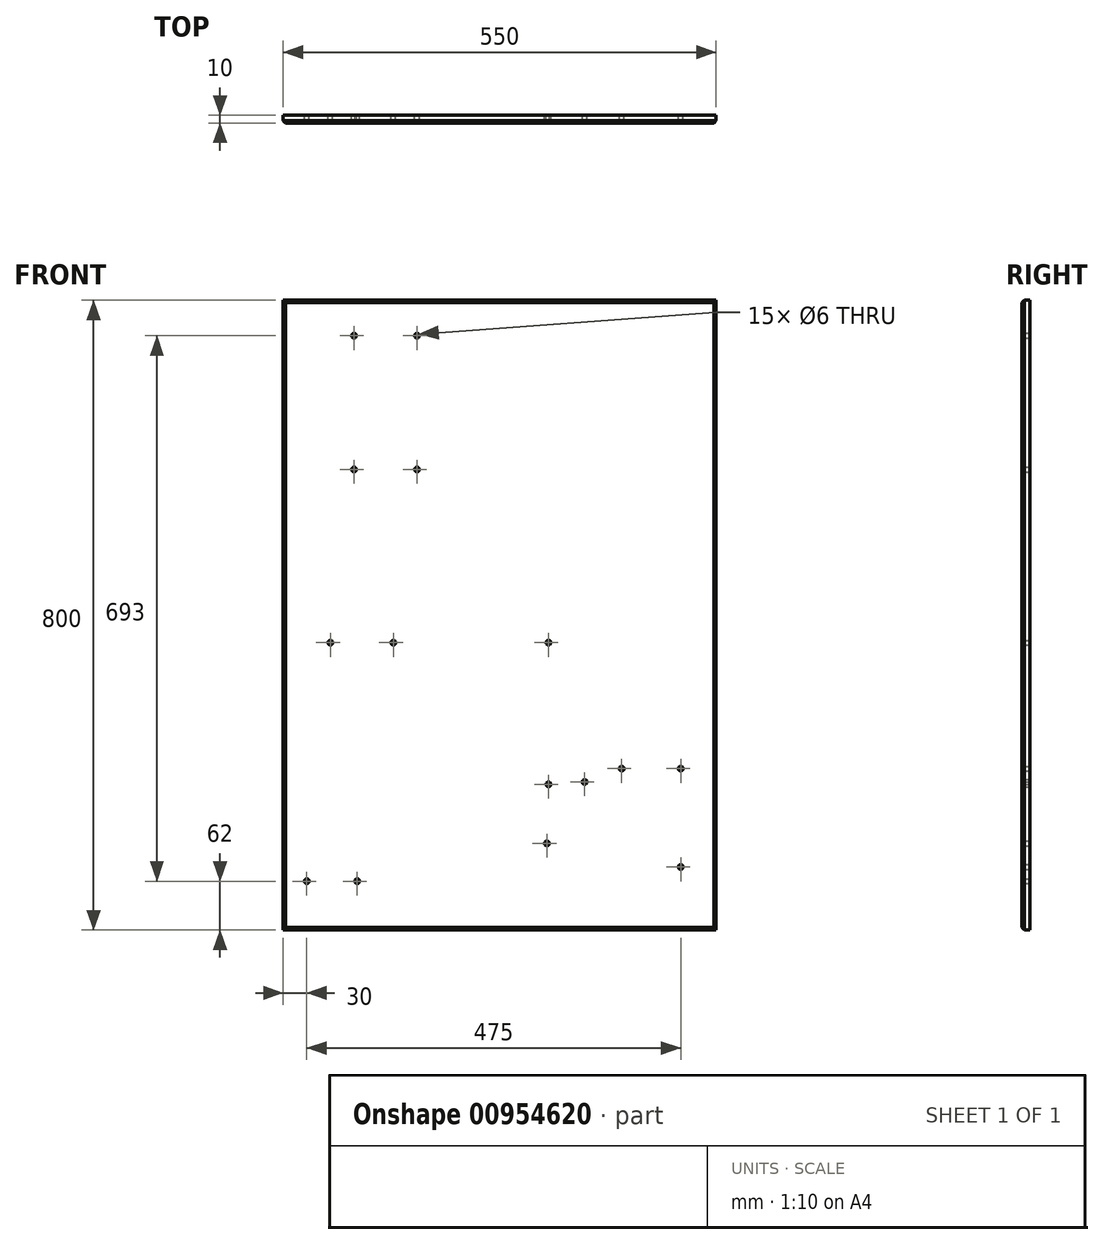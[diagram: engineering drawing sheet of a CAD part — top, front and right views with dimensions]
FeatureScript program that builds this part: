
annotation { "Feature Type Name" : "Feature", "Feature Type Description" : "" }
export const myFeature = defineFeature(function(context is Context, id is Id, definition is map)
    precondition{}
    {
        {
            var Q0;
            Q0=qCreatedBy(makeId("Front.planeOp"),FACE);
            var sketch = newSketch(context, id + "F0", { "sketchPlane" : qUnion([Q0])});
            skLineSegment(sketch, "E0.bottom", {"start": v(275, -400) * mm, "end": v(-275, -400) * mm});
            skLineSegment(sketch, "E0.top", {"start": v(275, 400) * mm, "end": v(-275, 400) * mm});
            skLineSegment(sketch, "E0.left", {"start": v(275, -400) * mm, "end": v(275, 400) * mm});
            skLineSegment(sketch, "E0.right", {"start": v(-275, -400) * mm, "end": v(-275, 400) * mm});
            skPoint(sketch, "E0.middle", {"position": v(0, 0) * mm});
            skLineSegment(sketch, "E1.bottom", {"start": v(-105, 355) * mm, "end": v(-185, 355) * mm, "construction": true});
            skLineSegment(sketch, "E1.top", {"start": v(-105, 185) * mm, "end": v(-185, 185) * mm, "construction": true});
            skLineSegment(sketch, "E1.left", {"start": v(-105, 355) * mm, "end": v(-105, 185) * mm, "construction": true});
            skLineSegment(sketch, "E1.right", {"start": v(-185, 355) * mm, "end": v(-185, 185) * mm, "construction": true});
            skCircle(sketch, "E2", {"center": v(-105, 355) * mm, "radius": 3 * mm});
            skCircle(sketch, "E3", {"center": v(-185, 355) * mm, "radius": 3 * mm});
            skCircle(sketch, "E4", {"center": v(-185, 185) * mm, "radius": 3 * mm});
            skCircle(sketch, "E5", {"center": v(-105, 185) * mm, "radius": 3 * mm});
            skCircle(sketch, "E6", {"center": v(-215, -35) * mm, "radius": 3 * mm});
            skCircle(sketch, "E7", {"center": v(-135, -35) * mm, "radius": 3 * mm});
            skCircle(sketch, "E8", {"center": v(-245, -338) * mm, "radius": 3 * mm});
            skCircle(sketch, "E9", {"center": v(-181, -338) * mm, "radius": 3 * mm});
            skCircle(sketch, "E10", {"center": v(62, -35) * mm, "radius": 3 * mm});
            skCircle(sketch, "E11", {"center": v(230, -195) * mm, "radius": 3 * mm});
            skCircle(sketch, "E12", {"center": v(155, -195) * mm, "radius": 3 * mm});
            skCircle(sketch, "E13", {"center": v(108, -212) * mm, "radius": 3 * mm});
            skCircle(sketch, "E14", {"center": v(62, -215) * mm, "radius": 3 * mm});
            skCircle(sketch, "E15", {"center": v(230, -320) * mm, "radius": 3 * mm});
            skCircle(sketch, "E16", {"center": v(60, -290) * mm, "radius": 3 * mm});
            skLineSegment(sketch, "E17", {"start": v(-135, -35) * mm, "end": v(-215, -35) * mm, "construction": true});
            skLineSegment(sketch, "E18", {"start": v(-181, -338) * mm, "end": v(-245, -338) * mm, "construction": true});
            skLineSegment(sketch, "E19", {"start": v(230, -195) * mm, "end": v(230, -320) * mm, "construction": true});
            skLineSegment(sketch, "E20", {"start": v(-135, -35) * mm, "end": v(62, -35) * mm, "construction": true});
            skLineSegment(sketch, "E21", {"start": v(155, -195) * mm, "end": v(230, -195) * mm, "construction": true});
            skLineSegment(sketch, "E22", {"start": v(62, -215) * mm, "end": v(62, -35) * mm, "construction": true});
            skSolve(sketch);
        }
        {
            var Q0;
            Q0 = qSketchRegion(id + "F0", true);
            extrude(context, id + "F1", {"entities" : qUnion([Q0]), "depth" : 10 * mm, "offsetDistance" : 25 * mm});
        }
        {
            var Q0;
            Q0=makeQuery(id+"F1.opExtrude","CAP_EDGE",EDGE,{"disambiguationData":[OSD([sQuery(id+"F0.wireOp",EDGE,"E0.right")])],"isStart":false});
            var Q1;
            Q1=makeQuery(id+"F1.opExtrude","CAP_EDGE",EDGE,{"disambiguationData":[OSD([sQuery(id+"F0.wireOp",EDGE,"E0.top")])],"isStart":false});
            var Q2;
            Q2=makeQuery(id+"F1.opExtrude","CAP_EDGE",EDGE,{"disambiguationData":[OSD([sQuery(id+"F0.wireOp",EDGE,"E0.left")])],"isStart":false});
            var Q3;
            Q3=makeQuery(id+"F1.opExtrude","CAP_EDGE",EDGE,{"disambiguationData":[OSD([sQuery(id+"F0.wireOp",EDGE,"E0.bottom")])],"isStart":false});
            chamfer(context, id + "F2", {"entities" : qUnion([Q0, Q1, Q2, Q3]), "width" : 3 * mm, "tangentPropagation" : true});
        }
    });
